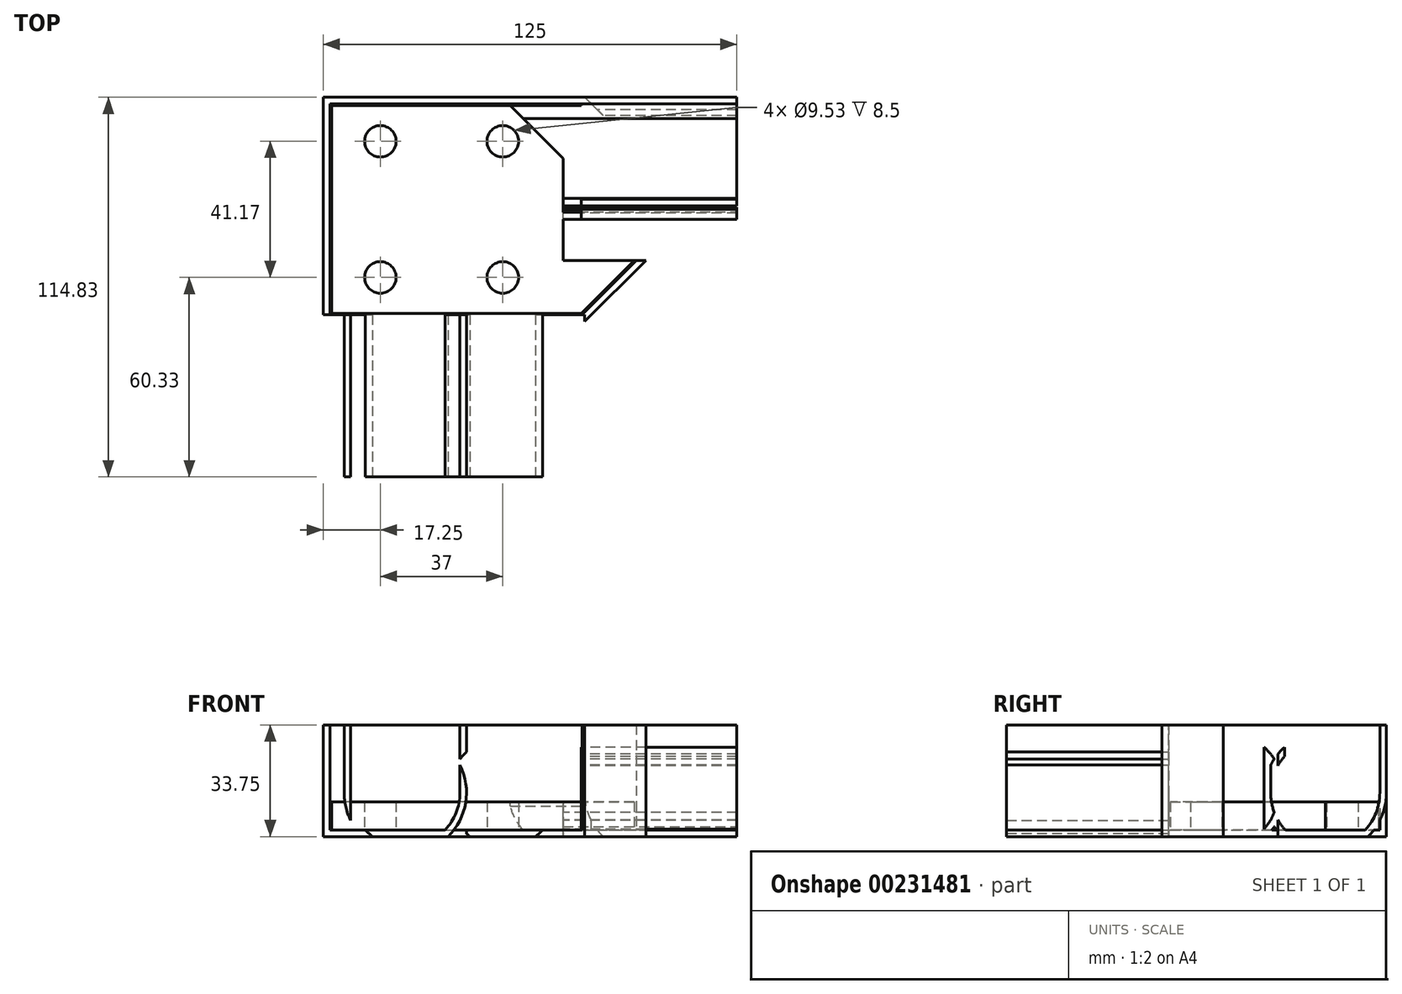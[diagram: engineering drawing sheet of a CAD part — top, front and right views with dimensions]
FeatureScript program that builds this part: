
annotation { "Feature Type Name" : "Feature", "Feature Type Description" : "" }
export const myFeature = defineFeature(function(context is Context, id is Id, definition is map)
    precondition{}
    {
        {
            var Q0;
            Q0=qCreatedBy(makeId("Top.planeOp"),FACE);
            var sketch = newSketch(context, id + "F0", { "sketchPlane" : qUnion([Q0])});
            skLineSegment(sketch, "E0.bottom", {"start": v(0, 0) * mm, "end": v(-75.5, 0) * mm});
            skLineSegment(sketch, "E0.top", {"start": v(0, 62.83) * mm, "end": v(-75.5, 62.83) * mm});
            skLineSegment(sketch, "E0.left", {"start": v(0, 0) * mm, "end": v(0, 62.83) * mm});
            skLineSegment(sketch, "E0.right", {"start": v(-75.5, 0) * mm, "end": v(-75.5, 62.83) * mm});
            skLineSegment(sketch, "E1", {"start": v(0, 62.83) * mm, "end": v(17, 45.83) * mm});
            skLineSegment(sketch, "E2", {"start": v(17, 45.83) * mm, "end": v(17, 17) * mm});
            skLineSegment(sketch, "E3", {"start": v(17, 17) * mm, "end": v(0, 0) * mm});
            skCircle(sketch, "E4", {"center": v(-23.75, 52) * mm, "radius": 4.76 * mm});
            skLineSegment(sketch, "E5", {"start": v(-75.5, 31.41) * mm, "end": v(0, 31.41) * mm, "construction": true});
            skCircle(sketch, "E6.1.0.0", {"center": v(-23.75, 10.83) * mm, "radius": 4.76 * mm});
            skLineSegment(sketch, "E6.direction1", {"start": v(-23.75, 52) * mm, "end": v(-23.75, 10.83) * mm, "construction": true});
            skCircle(sketch, "E7.1.0.0", {"center": v(-60.75, 52) * mm, "radius": 4.76 * mm});
            skCircle(sketch, "E7.1.0.1", {"center": v(-60.75, 10.83) * mm, "radius": 4.76 * mm});
            skLineSegment(sketch, "E7.direction1", {"start": v(-23.75, 52) * mm, "end": v(-60.75, 52) * mm, "construction": true});
            skSolve(sketch);
        }
        {
            var Q0;
            Q0=makeQuery(id+"F0.imprint","IMPRINT",FACE,{"disambiguationData":[TD([[makeQuery(id+"F0.imprint","IMPRINT",EDGE,{"derivedFrom":sQuery(id+"F0.wireOp",EDGE,"E0.bottom")}),-1.0]])]});
            var Q1;
            Q1=makeQuery(id+"F0.imprint","IMPRINT",FACE,{"disambiguationData":[TD([[makeQuery(id+"F0.imprint","IMPRINT",EDGE,{"derivedFrom":sQuery(id+"F0.wireOp",EDGE,"E0.left")}),-1.0]])]});
            extrude(context, id + "F1", {"entities" : qUnion([Q0, Q1]), "depth" : 10.5 * mm});
        }
        {
            var Q0;
            Q0=qCreatedBy(makeId("Top.planeOp"),FACE);
            var sketch = newSketch(context, id + "F2", { "sketchPlane" : qUnion([Q0])});
            skLineSegment(sketch, "E8.bottom", {"start": v(0.2, -0.5) * mm, "end": v(-76, -0.5) * mm});
            skLineSegment(sketch, "E8.top", {"start": v(0.2, 63.33) * mm, "end": v(-76, 63.33) * mm});
            skLineSegment(sketch, "E8.left", {"start": v(0.2, -0.5) * mm, "end": v(0.2, 63.33) * mm});
            skLineSegment(sketch, "E8.right", {"start": v(-76, -0.5) * mm, "end": v(-76, 63.33) * mm});
            skLineSegment(sketch, "E9", {"start": v(0.2, 63.33) * mm, "end": v(17.5, 46.04) * mm});
            skLineSegment(sketch, "E10", {"start": v(17.5, 46.04) * mm, "end": v(17.5, 16.8) * mm});
            skLineSegment(sketch, "E11", {"start": v(17.5, 16.8) * mm, "end": v(0.2, -0.5) * mm});
            skLineSegment(sketch, "E12", {"start": v(-76, 31.41) * mm, "end": v(0.2, 31.41) * mm, "construction": true});
            skLineSegment(sketch, "E13.bottom", {"start": v(1.04, -2.5) * mm, "end": v(-78, -2.5) * mm});
            skLineSegment(sketch, "E13.top", {"start": v(1.04, 65.33) * mm, "end": v(-78, 65.33) * mm});
            skLineSegment(sketch, "E13.left", {"start": v(1.04, -2.5) * mm, "end": v(1.04, 65.33) * mm});
            skLineSegment(sketch, "E13.right", {"start": v(-78, -2.5) * mm, "end": v(-78, 65.33) * mm});
            skLineSegment(sketch, "E14", {"start": v(1.04, 65.33) * mm, "end": v(19.5, 46.87) * mm});
            skLineSegment(sketch, "E15", {"start": v(19.5, 46.87) * mm, "end": v(19.5, 15.96) * mm});
            skLineSegment(sketch, "E16", {"start": v(19.5, 15.96) * mm, "end": v(1.04, -2.5) * mm});
            skSolve(sketch);
        }
        {
            var Q0;
            Q0 = qSketchRegion(id + "F2", true);
            var Q1;
            {var subQ0=sQuery(id+"F2.wireOp",EDGE,"E10");Q1=makeQuery(id+"F2.imprint","IMPRINT",FACE,{"disambiguationData":[TD([[makeQuery(id+"F2.imprint","IMPRINT",EDGE,{"derivedFrom":subQ0}),-1.0]])]});}
            var Q2;
            Q2=makeQuery(id+"F2.imprint","IMPRINT",FACE,{"disambiguationData":[TD([[makeQuery(id+"F2.imprint","IMPRINT",EDGE,{"derivedFrom":sQuery(id+"F2.wireOp",EDGE,"E8.bottom")}),-1.0]])]});
            var Q3;
            {var subQ0=sQuery(id+"F2.wireOp",EDGE,"E8.left");Q3=makeQuery(id+"F2.imprint","IMPRINT",FACE,{"disambiguationData":[TD([[makeQuery(id+"F2.imprint","IMPRINT",EDGE,{"derivedFrom":subQ0}),-1.0]])]});}
            extrude(context, id + "F3", {"entities" : qUnion([Q0, Q1, Q2, Q3]), "depth" : 2 * mm});
        }
        {
            var Q0;
            {var subQ5=sQuery(id+"F2.wireOp",EDGE,"E8.bottom");Q0=makeQuery(id+"F2.imprint","IMPRINT",FACE,{"disambiguationData":[TD([[makeQuery(id+"F2.imprint","IMPRINT",EDGE,{"derivedFrom":subQ5}),1.0]])]});}
            var Q1;
            {var subQ4=sQuery(id+"F2.wireOp",EDGE,"E10");Q1=makeQuery(id+"F2.imprint","IMPRINT",FACE,{"disambiguationData":[TD([[makeQuery(id+"F2.imprint","IMPRINT",EDGE,{"derivedFrom":subQ4}),1.0]])]});}
            extrude(context, id + "F4", {"entities" : qUnion([Q0, Q1]), "depth" : (21 + 10.75 + 2) * mm});
        }
        {
            var Q0;
            Q0=makeQuery(id+"F3.opExtrude","SWEPT_BODY",BODY,{"disambiguationData":[OSD([sQuery(id+"F2.wireOp",EDGE,"E13.bottom"),sQuery(id+"F2.wireOp",EDGE,"E13.top"),sQuery(id+"F2.wireOp",EDGE,"E13.right"),sQuery(id+"F2.wireOp",EDGE,"E14"),sQuery(id+"F2.wireOp",EDGE,"E15"),sQuery(id+"F2.wireOp",EDGE,"E16")])]});
            var Q1;
            Q1=makeQuery(id+"F4.opExtrude","SWEPT_BODY",BODY,{"disambiguationData":[OSD([sQuery(id+"F2.wireOp",EDGE,"E8.bottom"),sQuery(id+"F2.wireOp",EDGE,"E8.top"),sQuery(id+"F2.wireOp",EDGE,"E8.right"),sQuery(id+"F2.wireOp",EDGE,"E9"),sQuery(id+"F2.wireOp",EDGE,"E10"),sQuery(id+"F2.wireOp",EDGE,"E11"),sQuery(id+"F2.wireOp",EDGE,"E13.bottom"),sQuery(id+"F2.wireOp",EDGE,"E13.top"),sQuery(id+"F2.wireOp",EDGE,"E13.right"),sQuery(id+"F2.wireOp",EDGE,"E14"),sQuery(id+"F2.wireOp",EDGE,"E15"),sQuery(id+"F2.wireOp",EDGE,"E16")])]});
            booleanBodies(context, id + "F5", {"operationType" : BooleanOperationType.UNION, "tools" : qUnion([Q0, Q1])});
        }
        {
            var Q0;
            {var subQ0=sQuery(id+"F2.wireOp",EDGE,"E13.bottom");Q0=makeQuery(id+"F5.opBoolean","MERGE",FACE,{"derivedFrom":[makeQuery(id+"F3.opExtrude","SWEPT_FACE",FACE,{"disambiguationData":[OSD([subQ0])]}),makeQuery(id+"F4.opExtrude","SWEPT_FACE",FACE,{"disambiguationData":[OSD([subQ0])]})]});}
            var sketch = newSketch(context, id + "F6", { "sketchPlane" : qUnion([Q0])});
            skPoint(sketch, "E17.0", {"position": v(-23.75, 0) * mm});
            skPoint(sketch, "E18.0", {"position": v(-60.75, 0) * mm});
            skCircle(sketch, "E19", {"center": v(-23.75, 13.24) * mm, "radius": 18.5 * mm});
            skLineSegment(sketch, "E20", {"start": v(-23.75, 0) * mm, "end": v(-23.75, 33.75) * mm, "construction": true});
            skLineSegment(sketch, "E21", {"start": v(-42.25, 0) * mm, "end": v(-42.25, 33.75) * mm, "construction": true});
            skLineSegment(sketch, "E22", {"start": v(-60.75, 0) * mm, "end": v(-23.75, 0) * mm});
            skLineSegment(sketch, "E23", {"start": v(-42.25, 0) * mm, "end": v(-42.25, 33.75) * mm});
            skLineSegment(sketch, "E24", {"start": v(-5.25, 0) * mm, "end": v(-5.25, 33.75) * mm});
            skCircle(sketch, "E25", {"center": v(-23.75, 13.24) * mm, "radius": 16.5 * mm});
            skLineSegment(sketch, "E26", {"start": v(-40.25, 33.75) * mm, "end": v(-40.25, 0) * mm});
            skLineSegment(sketch, "E27", {"start": v(-7.25, 33.75) * mm, "end": v(-7.25, 0) * mm});
            skLineSegment(sketch, "E28", {"start": v(-42.25, 13.24) * mm, "end": v(-5.25, 13.24) * mm});
            skLineSegment(sketch, "E29", {"start": v(-35.83, 2) * mm, "end": v(-11.67, 2) * mm});
            skLineSegment(sketch, "E30", {"start": v(-38.48, 33.75) * mm, "end": v(-38.48, 0) * mm, "construction": true});
            skLineSegment(sketch, "E31.MirrorCS", {"start": v(-34.71, 0) * mm, "end": v(-34.71, 33.75) * mm});
            skLineSegment(sketch, "E32.MirrorCS", {"start": v(-41.13, 2) * mm, "end": v(-65.3, 2) * mm});
            skLineSegment(sketch, "E33.MirrorCS", {"start": v(-69.71, 33.75) * mm, "end": v(-69.71, 0) * mm});
            skLineSegment(sketch, "E34.MirrorCS", {"start": v(-36.71, 33.75) * mm, "end": v(-36.71, 0) * mm});
            skPoint(sketch, "E35.MirrorP", {"position": v(-53.21, 0) * mm});
            skCircle(sketch, "E36.MirrorC", {"center": v(-53.21, 13.24) * mm, "radius": 16.5 * mm});
            skLineSegment(sketch, "E37.MirrorCS", {"start": v(-71.71, 0) * mm, "end": v(-71.71, 33.75) * mm});
            skCircle(sketch, "E38.MirrorC", {"center": v(-53.21, 13.24) * mm, "radius": 18.5 * mm});
            skLineSegment(sketch, "E39.MirrorCS", {"start": v(-53.21, 0) * mm, "end": v(-53.21, 33.75) * mm, "construction": true});
            skLineSegment(sketch, "E40.MirrorCS", {"start": v(-34.71, 0) * mm, "end": v(-34.71, 33.75) * mm, "construction": true});
            skLineSegment(sketch, "E41.MirrorCS", {"start": v(-34.71, 13.24) * mm, "end": v(-71.71, 13.24) * mm});
            skSolve(sketch);
        }
        {
            var Q0;
            {var subQ0=sQuery(id+"F2.wireOp",EDGE,"E13.right");Q0=makeQuery(id+"F5.opBoolean","MERGE",FACE,{"derivedFrom":[makeQuery(id+"F3.opExtrude","SWEPT_FACE",FACE,{"disambiguationData":[OSD([subQ0])]}),makeQuery(id+"F4.opExtrude","SWEPT_FACE",FACE,{"disambiguationData":[OSD([subQ0])]})]});}
            cPlane(context, id + "F7", {"entities" : qUnion([Q0]), "cplaneType" : CPlaneType.OFFSET, "offset" : 78 * mm, "oppositeDirection" : true, "width" : 150 * mm, "height" : 150 * mm});
        }
        {
            var Q0;
            Q0=qCreatedBy(id+"F7.planeOp",FACE);
            var sketch = newSketch(context, id + "F8", { "sketchPlane" : qUnion([Q0])});
            skPoint(sketch, "E42.0", {"position": v(0.5, 33.75) * mm});
            skPoint(sketch, "E43.0", {"position": v(-63.33, 33.75) * mm});
            skCircle(sketch, "E44", {"center": v(-16, 13.24) * mm, "radius": 18.5 * mm});
            skLineSegment(sketch, "E45", {"start": v(0.5, 33.75) * mm, "end": v(0.5, 0) * mm});
            skLineSegment(sketch, "E46.bottom", {"start": v(-34.5, 33.75) * mm, "end": v(-32.5, 33.75) * mm});
            skLineSegment(sketch, "E46.top", {"start": v(-34.5, 0) * mm, "end": v(-32.5, 0) * mm});
            skLineSegment(sketch, "E46.left", {"start": v(-34.5, 33.75) * mm, "end": v(-34.5, 0) * mm});
            skLineSegment(sketch, "E46.right", {"start": v(-32.5, 33.75) * mm, "end": v(-32.5, 0) * mm});
            skLineSegment(sketch, "E47.bottom", {"start": v(-32.5, 2) * mm, "end": v(0.5, 2) * mm});
            skLineSegment(sketch, "E47.top", {"start": v(-32.5, 0) * mm, "end": v(0.5, 0) * mm});
            skLineSegment(sketch, "E47.left", {"start": v(-32.5, 2) * mm, "end": v(-32.5, 0) * mm});
            skLineSegment(sketch, "E47.right", {"start": v(0.5, 2) * mm, "end": v(0.5, 0) * mm});
            skCircle(sketch, "E48", {"center": v(-16, 13.24) * mm, "radius": 16.5 * mm});
            skLineSegment(sketch, "E49", {"start": v(0.5, 33.75) * mm, "end": v(2.5, 33.75) * mm});
            skLineSegment(sketch, "E50", {"start": v(2.5, 33.75) * mm, "end": v(2.5, 0) * mm});
            skLineSegment(sketch, "E51", {"start": v(2.5, 0) * mm, "end": v(0.5, 0) * mm});
            skLineSegment(sketch, "E52", {"start": v(0.5, 33.75) * mm, "end": v(-32.5, 33.75) * mm});
            skLineSegment(sketch, "E53", {"start": v(-31.41, 34.55) * mm, "end": v(-31.41, 0) * mm, "construction": true});
            skLineSegment(sketch, "E54.MirrorCS", {"start": v(-30.33, 2) * mm, "end": v(-30.33, 0) * mm});
            skLineSegment(sketch, "E55.MirrorCS", {"start": v(-63.33, 33.75) * mm, "end": v(-65.33, 33.75) * mm});
            skLineSegment(sketch, "E56.MirrorCS", {"start": v(-63.33, 2) * mm, "end": v(-63.33, 0) * mm});
            skLineSegment(sketch, "E57.MirrorCS", {"start": v(-28.33, 33.75) * mm, "end": v(-30.33, 33.75) * mm});
            skLineSegment(sketch, "E58.MirrorCS", {"start": v(-30.33, 2) * mm, "end": v(-63.33, 2) * mm});
            skLineSegment(sketch, "E59.MirrorCS", {"start": v(-28.33, 33.75) * mm, "end": v(-28.33, 0) * mm});
            skCircle(sketch, "E60.MirrorC", {"center": v(-46.83, 13.24) * mm, "radius": 16.5 * mm});
            skLineSegment(sketch, "E61.MirrorCS", {"start": v(-65.33, 33.75) * mm, "end": v(-65.33, 0) * mm});
            skLineSegment(sketch, "E62.MirrorCS", {"start": v(-63.33, 33.75) * mm, "end": v(-30.33, 33.75) * mm});
            skLineSegment(sketch, "E63.MirrorCS", {"start": v(-30.33, 0) * mm, "end": v(-63.33, 0) * mm});
            skLineSegment(sketch, "E64.MirrorCS", {"start": v(-28.33, 0) * mm, "end": v(-30.33, 0) * mm});
            skLineSegment(sketch, "E65.MirrorCS", {"start": v(-63.33, 33.75) * mm, "end": v(-63.33, 0) * mm});
            skCircle(sketch, "E66.MirrorC", {"center": v(-46.83, 13.24) * mm, "radius": 18.5 * mm});
            skLineSegment(sketch, "E67.MirrorCS", {"start": v(-65.33, 0) * mm, "end": v(-63.33, 0) * mm});
            skLineSegment(sketch, "E68.MirrorCS", {"start": v(-30.33, 33.75) * mm, "end": v(-30.33, 0) * mm});
            skSolve(sketch);
        }
        {
            var Q0;
            {var subQ0=sQuery(id+"F6.wireOp",EDGE,"E33.MirrorCS");var subQ1=makeQuery(id+"F4.opExtrude","CAP_EDGE",EDGE,{"disambiguationData":[OSD([sQuery(id+"F2.wireOp",EDGE,"E13.bottom")])],"isStart":false});var subQ2=makeQuery(id+"F6.imprint","INTERSECT",VERTEX,{"derivedFrom":[subQ1,subQ0]});Q0=makeQuery(id+"F6.imprint","IMPRINT",FACE,{"disambiguationData":[TD([[makeQuery(id+"F6.imprint","IMPRINT",EDGE,{"disambiguationData":[TD([[subQ2,-1.0]])],"derivedFrom":subQ0}),-1.0]])]});}
            var Q1;
            {var subQ0=sQuery(id+"F6.wireOp",EDGE,"E38.MirrorC");var subQ1=sQuery(id+"F6.wireOp",EDGE,"E33.MirrorCS");var subQ2=makeQuery(id+"F6.imprint","INTERSECT",VERTEX,{"disambiguationData":[OD(0.0)],"derivedFrom":[subQ1,subQ0]});Q1=makeQuery(id+"F6.imprint","IMPRINT",FACE,{"disambiguationData":[TD([[makeQuery(id+"F6.imprint","IMPRINT",EDGE,{"disambiguationData":[TD([[subQ2,-1.0]])],"derivedFrom":subQ1}),-1.0]])]});}
            var Q2;
            {var subQ0=sQuery(id+"F6.wireOp",EDGE,"E38.MirrorC");var subQ1=sQuery(id+"F6.wireOp",EDGE,"E33.MirrorCS");var subQ2=makeQuery(id+"F6.imprint","INTERSECT",VERTEX,{"disambiguationData":[OD(1.0)],"derivedFrom":[subQ1,subQ0]});Q2=makeQuery(id+"F6.imprint","IMPRINT",FACE,{"disambiguationData":[TD([[makeQuery(id+"F6.imprint","IMPRINT",EDGE,{"disambiguationData":[TD([[subQ2,1.0]])],"derivedFrom":subQ1}),-1.0]])]});}
            var Q3;
            {var subQ5=sQuery(id+"F6.wireOp",EDGE,"E36.MirrorC");var subQ7=makeQuery(id+"F6.imprint","INTERSECT",VERTEX,{"disambiguationData":[OD(1.0)],"derivedFrom":[sQuery(id+"F6.wireOp",EDGE,"E32.MirrorCS"),subQ5]});Q3=makeQuery(id+"F6.imprint","IMPRINT",FACE,{"disambiguationData":[TD([[makeQuery(id+"F6.imprint","IMPRINT",EDGE,{"disambiguationData":[TD([[subQ7,1.0]])],"derivedFrom":subQ5}),1.0]])]});}
            var Q4;
            {var subQ1=sQuery(id+"F6.wireOp",EDGE,"E22");var subQ8=makeQuery(id+"F3.opExtrude","CAP_EDGE",EDGE,{"disambiguationData":[OSD([sQuery(id+"F2.wireOp",EDGE,"E13.bottom")])],"isStart":true});var subQ9=makeQuery(id+"F6.imprint","INTERSECT",VERTEX,{"disambiguationData":[OD(1.0)],"derivedFrom":[subQ8,subQ1]});Q4=makeQuery(id+"F6.imprint","IMPRINT",FACE,{"disambiguationData":[TD([[makeQuery(id+"F6.imprint","IMPRINT",EDGE,{"disambiguationData":[TD([[subQ9,1.0]])],"derivedFrom":subQ1}),-1.0]])]});}
            var Q5;
            {var subQ0=sQuery(id+"F6.wireOp",EDGE,"E36.MirrorC");var subQ1=sQuery(id+"F6.wireOp",EDGE,"E23");var subQ2=makeQuery(id+"F6.imprint","INTERSECT",VERTEX,{"disambiguationData":[OD(0.0)],"derivedFrom":[subQ1,subQ0]});Q5=makeQuery(id+"F6.imprint","IMPRINT",FACE,{"disambiguationData":[TD([[makeQuery(id+"F6.imprint","IMPRINT",EDGE,{"disambiguationData":[TD([[subQ2,-1.0]])],"derivedFrom":subQ1}),-1.0]])]});}
            var Q6;
            {var subQ6=sQuery(id+"F6.wireOp",EDGE,"E23");var subQ7=sQuery(id+"F6.wireOp",EDGE,"E22");var subQ8=makeQuery(id+"F6.imprint","INTERSECT",VERTEX,{"derivedFrom":[subQ7,subQ6]});Q6=makeQuery(id+"F6.imprint","IMPRINT",FACE,{"disambiguationData":[TD([[makeQuery(id+"F6.imprint","IMPRINT",EDGE,{"disambiguationData":[TD([[subQ8,1.0]])],"derivedFrom":subQ7}),-1.0]])]});}
            var Q7;
            {var subQ0=sQuery(id+"F6.wireOp",EDGE,"E23");var subQ1=sQuery(id+"F6.wireOp",EDGE,"E22");var subQ2=makeQuery(id+"F6.imprint","INTERSECT",VERTEX,{"derivedFrom":[subQ1,subQ0]});Q7=makeQuery(id+"F6.imprint","IMPRINT",FACE,{"disambiguationData":[TD([[makeQuery(id+"F6.imprint","IMPRINT",EDGE,{"disambiguationData":[TD([[subQ2,-1.0]])],"derivedFrom":subQ1}),-1.0]])]});}
            var Q8;
            {var subQ0=sQuery(id+"F6.wireOp",EDGE,"E36.MirrorC");var subQ1=sQuery(id+"F6.wireOp",EDGE,"E19");var subQ2=makeQuery(id+"F6.imprint","INTERSECT",VERTEX,{"disambiguationData":[OD(1.0)],"derivedFrom":[subQ1,subQ0]});Q8=makeQuery(id+"F6.imprint","IMPRINT",FACE,{"disambiguationData":[TD([[makeQuery(id+"F6.imprint","IMPRINT",EDGE,{"disambiguationData":[TD([[subQ2,-1.0]])],"derivedFrom":subQ1}),-1.0]])]});}
            var Q9;
            {var subQ0=sQuery(id+"F6.wireOp",EDGE,"E36.MirrorC");var subQ1=sQuery(id+"F6.wireOp",EDGE,"E19");var subQ2=makeQuery(id+"F6.imprint","INTERSECT",VERTEX,{"disambiguationData":[OD(1.0)],"derivedFrom":[subQ1,subQ0]});Q9=makeQuery(id+"F6.imprint","IMPRINT",FACE,{"disambiguationData":[TD([[makeQuery(id+"F6.imprint","IMPRINT",EDGE,{"disambiguationData":[TD([[subQ2,-1.0]])],"derivedFrom":subQ1}),1.0]])]});}
            var Q10;
            {var subQ0=sQuery(id+"F6.wireOp",EDGE,"E36.MirrorC");var subQ1=sQuery(id+"F6.wireOp",EDGE,"E25");var subQ2=makeQuery(id+"F6.imprint","INTERSECT",VERTEX,{"disambiguationData":[OD(1.0)],"derivedFrom":[subQ1,subQ0]});Q10=makeQuery(id+"F6.imprint","IMPRINT",FACE,{"disambiguationData":[TD([[makeQuery(id+"F6.imprint","IMPRINT",EDGE,{"disambiguationData":[TD([[subQ2,-1.0]])],"derivedFrom":subQ1}),1.0]])]});}
            var Q11;
            {var subQ0=sQuery(id+"F6.wireOp",EDGE,"E38.MirrorC");var subQ1=sQuery(id+"F6.wireOp",EDGE,"E34.MirrorCS");var subQ2=makeQuery(id+"F6.imprint","INTERSECT",VERTEX,{"disambiguationData":[OD(1.0)],"derivedFrom":[subQ1,subQ0]});Q11=makeQuery(id+"F6.imprint","IMPRINT",FACE,{"disambiguationData":[TD([[makeQuery(id+"F6.imprint","IMPRINT",EDGE,{"disambiguationData":[TD([[subQ2,1.0]])],"derivedFrom":subQ1}),1.0]])]});}
            var Q12;
            {var subQ0=sQuery(id+"F6.wireOp",EDGE,"E38.MirrorC");var subQ1=sQuery(id+"F6.wireOp",EDGE,"E34.MirrorCS");var subQ2=makeQuery(id+"F6.imprint","INTERSECT",VERTEX,{"disambiguationData":[OD(0.0)],"derivedFrom":[subQ1,subQ0]});Q12=makeQuery(id+"F6.imprint","IMPRINT",FACE,{"disambiguationData":[TD([[makeQuery(id+"F6.imprint","IMPRINT",EDGE,{"disambiguationData":[TD([[subQ2,-1.0]])],"derivedFrom":subQ1}),1.0]])]});}
            var Q13;
            {var subQ0=sQuery(id+"F6.wireOp",EDGE,"E31.MirrorCS");var subQ1=sQuery(id+"F6.wireOp",EDGE,"E25");var subQ2=makeQuery(id+"F6.imprint","INTERSECT",VERTEX,{"disambiguationData":[OD(0.0)],"derivedFrom":[subQ1,subQ0]});Q13=makeQuery(id+"F6.imprint","IMPRINT",FACE,{"disambiguationData":[TD([[makeQuery(id+"F6.imprint","IMPRINT",EDGE,{"disambiguationData":[TD([[subQ2,-1.0]])],"derivedFrom":subQ1}),1.0]])]});}
            var Q14;
            {var subQ0=sQuery(id+"F6.wireOp",EDGE,"E31.MirrorCS");var subQ1=sQuery(id+"F6.wireOp",EDGE,"E19");var subQ2=makeQuery(id+"F6.imprint","INTERSECT",VERTEX,{"derivedFrom":[subQ1,subQ0]});Q14=makeQuery(id+"F6.imprint","IMPRINT",FACE,{"disambiguationData":[TD([[makeQuery(id+"F6.imprint","IMPRINT",EDGE,{"disambiguationData":[TD([[subQ2,-1.0]])],"derivedFrom":subQ1}),1.0]])]});}
            var Q15;
            {var subQ0=sQuery(id+"F6.wireOp",EDGE,"E31.MirrorCS");var subQ1=sQuery(id+"F6.wireOp",EDGE,"E19");var subQ2=makeQuery(id+"F6.imprint","INTERSECT",VERTEX,{"derivedFrom":[subQ1,subQ0]});Q15=makeQuery(id+"F6.imprint","IMPRINT",FACE,{"disambiguationData":[TD([[makeQuery(id+"F6.imprint","IMPRINT",EDGE,{"disambiguationData":[TD([[subQ2,-1.0]])],"derivedFrom":subQ1}),-1.0]])]});}
            extrude(context, id + "F9", {"entities" : qUnion([Q0, Q1, Q2, Q3, Q4, Q5, Q6, Q7, Q8, Q9, Q10, Q11, Q12, Q13, Q14, Q15]), "operationType" : NewBodyOperationType.ADD, "depth" : 47 * mm});
        }
        {
            var Q0;
            {var subQ0=sQuery(id+"F8.wireOp",EDGE,"E66.MirrorC");var subQ1=sQuery(id+"F8.wireOp",EDGE,"E48");var subQ2=makeQuery(id+"F8.imprint","INTERSECT",VERTEX,{"disambiguationData":[OD(0.0)],"derivedFrom":[subQ1,subQ0]});Q0=makeQuery(id+"F8.imprint","IMPRINT",FACE,{"disambiguationData":[TD([[makeQuery(id+"F8.imprint","IMPRINT",EDGE,{"disambiguationData":[TD([[subQ2,-1.0]])],"derivedFrom":subQ1}),1.0]])]});}
            var Q1;
            {var subQ0=sQuery(id+"F8.wireOp",EDGE,"E60.MirrorC");var subQ1=sQuery(id+"F8.wireOp",EDGE,"E48");var subQ2=makeQuery(id+"F8.imprint","INTERSECT",VERTEX,{"disambiguationData":[OD(1.0)],"derivedFrom":[subQ1,subQ0]});Q1=makeQuery(id+"F8.imprint","IMPRINT",FACE,{"disambiguationData":[TD([[makeQuery(id+"F8.imprint","IMPRINT",EDGE,{"disambiguationData":[TD([[subQ2,-1.0]])],"derivedFrom":subQ1}),1.0]])]});}
            var Q2;
            {var subQ0=sQuery(id+"F8.wireOp",EDGE,"E59.MirrorCS");var subQ1=sQuery(id+"F8.wireOp",EDGE,"E48");var subQ2=makeQuery(id+"F8.imprint","INTERSECT",VERTEX,{"disambiguationData":[OD(0.0)],"derivedFrom":[subQ1,subQ0]});Q2=makeQuery(id+"F8.imprint","IMPRINT",FACE,{"disambiguationData":[TD([[makeQuery(id+"F8.imprint","IMPRINT",EDGE,{"disambiguationData":[TD([[subQ2,-1.0]])],"derivedFrom":subQ1}),1.0]])]});}
            var Q3;
            {var subQ0=sQuery(id+"F8.wireOp",EDGE,"E59.MirrorCS");var subQ1=sQuery(id+"F8.wireOp",EDGE,"E44");var subQ2=makeQuery(id+"F8.imprint","INTERSECT",VERTEX,{"derivedFrom":[subQ1,subQ0]});Q3=makeQuery(id+"F8.imprint","IMPRINT",FACE,{"disambiguationData":[TD([[makeQuery(id+"F8.imprint","IMPRINT",EDGE,{"disambiguationData":[TD([[subQ2,-1.0]])],"derivedFrom":subQ1}),1.0]])]});}
            var Q4;
            {var subQ5=sQuery(id+"F8.wireOp",EDGE,"E57.MirrorCS");Q4=makeQuery(id+"F8.imprint","IMPRINT",FACE,{"disambiguationData":[TD([[makeQuery(id+"F8.imprint","IMPRINT",EDGE,{"derivedFrom":subQ5}),1.0]])]});}
            var Q5;
            {var subQ5=sQuery(id+"F8.wireOp",EDGE,"E46.right");var subQ6=sQuery(id+"F8.wireOp",EDGE,"E44");var subQ7=makeQuery(id+"F8.imprint","INTERSECT",VERTEX,{"disambiguationData":[OD(1.0)],"derivedFrom":[subQ6,subQ5]});Q5=makeQuery(id+"F8.imprint","IMPRINT",FACE,{"disambiguationData":[TD([[makeQuery(id+"F8.imprint","IMPRINT",EDGE,{"disambiguationData":[TD([[subQ7,-1.0]])],"derivedFrom":subQ6}),1.0]])]});}
            var Q6;
            {var subQ5=sQuery(id+"F8.wireOp",EDGE,"E44");var subQ7=sQuery(id+"F8.wireOp",EDGE,"E60.MirrorC");var subQ9=makeQuery(id+"F8.imprint","INTERSECT",VERTEX,{"disambiguationData":[OD(1.0)],"derivedFrom":[subQ5,subQ7]});Q6=makeQuery(id+"F8.imprint","IMPRINT",FACE,{"disambiguationData":[TD([[makeQuery(id+"F8.imprint","IMPRINT",EDGE,{"disambiguationData":[TD([[subQ9,-1.0]])],"derivedFrom":subQ5}),-1.0]])]});}
            var Q7;
            {var subQ0=sQuery(id+"F8.wireOp",EDGE,"E46.right");var subQ1=sQuery(id+"F8.wireOp",EDGE,"E44");var subQ2=makeQuery(id+"F8.imprint","INTERSECT",VERTEX,{"disambiguationData":[OD(1.0)],"derivedFrom":[subQ1,subQ0]});Q7=makeQuery(id+"F8.imprint","IMPRINT",FACE,{"disambiguationData":[TD([[makeQuery(id+"F8.imprint","IMPRINT",EDGE,{"disambiguationData":[TD([[subQ2,-1.0]])],"derivedFrom":subQ1}),-1.0]])]});}
            var Q8;
            {var subQ0=sQuery(id+"F8.wireOp",EDGE,"E63.MirrorCS");var subQ1=sQuery(id+"F8.wireOp",EDGE,"E46.left");var subQ2=makeQuery(id+"F8.imprint","INTERSECT",VERTEX,{"derivedFrom":[subQ1,subQ0]});Q8=makeQuery(id+"F8.imprint","IMPRINT",FACE,{"disambiguationData":[TD([[makeQuery(id+"F8.imprint","IMPRINT",EDGE,{"disambiguationData":[TD([[subQ2,1.0]])],"derivedFrom":subQ1}),1.0]])]});}
            var Q9;
            {var subQ0=sQuery(id+"F8.wireOp",EDGE,"E63.MirrorCS");var subQ1=sQuery(id+"F8.wireOp",EDGE,"E46.left");var subQ2=makeQuery(id+"F8.imprint","INTERSECT",VERTEX,{"derivedFrom":[subQ1,subQ0]});Q9=makeQuery(id+"F8.imprint","IMPRINT",FACE,{"disambiguationData":[TD([[makeQuery(id+"F8.imprint","IMPRINT",EDGE,{"disambiguationData":[TD([[subQ2,1.0]])],"derivedFrom":subQ1}),-1.0]])]});}
            var Q10;
            {var subQ0=sQuery(id+"F8.wireOp",EDGE,"E60.MirrorC");var subQ1=sQuery(id+"F8.wireOp",EDGE,"E58.MirrorCS");var subQ2=makeQuery(id+"F8.imprint","INTERSECT",VERTEX,{"disambiguationData":[OD(0.0)],"derivedFrom":[subQ1,subQ0]});Q10=makeQuery(id+"F8.imprint","IMPRINT",FACE,{"disambiguationData":[TD([[makeQuery(id+"F8.imprint","IMPRINT",EDGE,{"disambiguationData":[TD([[subQ2,-1.0]])],"derivedFrom":subQ1}),1.0]])]});}
            var Q11;
            {var subQ0=sQuery(id+"F8.wireOp",EDGE,"E60.MirrorC");var subQ1=sQuery(id+"F8.wireOp",EDGE,"E58.MirrorCS");var subQ2=makeQuery(id+"F8.imprint","INTERSECT",VERTEX,{"disambiguationData":[OD(1.0)],"derivedFrom":[subQ1,subQ0]});Q11=makeQuery(id+"F8.imprint","IMPRINT",FACE,{"disambiguationData":[TD([[makeQuery(id+"F8.imprint","IMPRINT",EDGE,{"disambiguationData":[TD([[subQ2,-1.0]])],"derivedFrom":subQ1}),1.0]])]});}
            var Q12;
            {var subQ0=sQuery(id+"F8.wireOp",EDGE,"E60.MirrorC");var subQ1=sQuery(id+"F8.wireOp",EDGE,"E58.MirrorCS");var subQ2=makeQuery(id+"F8.imprint","INTERSECT",VERTEX,{"disambiguationData":[OD(1.0)],"derivedFrom":[subQ1,subQ0]});Q12=makeQuery(id+"F8.imprint","IMPRINT",FACE,{"disambiguationData":[TD([[makeQuery(id+"F8.imprint","IMPRINT",EDGE,{"disambiguationData":[TD([[subQ2,-1.0]])],"derivedFrom":subQ1}),-1.0]])]});}
            var Q13;
            {var subQ0=sQuery(id+"F8.wireOp",EDGE,"E65.MirrorCS");var subQ1=makeQuery(id+"F8.imprint","INTERSECT",VERTEX,{"derivedFrom":[sQuery(id+"F8.wireOp",EDGE,"E60.MirrorC"),subQ0]});Q13=makeQuery(id+"F8.imprint","IMPRINT",FACE,{"disambiguationData":[TD([[makeQuery(id+"F8.imprint","IMPRINT",EDGE,{"disambiguationData":[TD([[subQ1,1.0]])],"derivedFrom":subQ0}),-1.0]])]});}
            var Q14;
            {var subQ0=sQuery(id+"F8.wireOp",EDGE,"E55.MirrorCS");Q14=makeQuery(id+"F8.imprint","IMPRINT",FACE,{"disambiguationData":[TD([[makeQuery(id+"F8.imprint","IMPRINT",EDGE,{"derivedFrom":subQ0}),1.0]])]});}
            var Q15;
            {var subQ0=sQuery(id+"F8.wireOp",EDGE,"E60.MirrorC");var subQ1=sQuery(id+"F8.wireOp",EDGE,"E46.left");var subQ2=makeQuery(id+"F8.imprint","INTERSECT",VERTEX,{"disambiguationData":[OD(1.0)],"derivedFrom":[subQ1,subQ0]});Q15=makeQuery(id+"F8.imprint","IMPRINT",FACE,{"disambiguationData":[TD([[makeQuery(id+"F8.imprint","IMPRINT",EDGE,{"disambiguationData":[TD([[subQ2,-1.0]])],"derivedFrom":subQ1}),-1.0]])]});}
            var Q16;
            {var subQ0=sQuery(id+"F8.wireOp",EDGE,"E66.MirrorC");var subQ1=sQuery(id+"F8.wireOp",EDGE,"E48");var subQ2=makeQuery(id+"F8.imprint","INTERSECT",VERTEX,{"disambiguationData":[OD(0.0)],"derivedFrom":[subQ1,subQ0]});Q16=makeQuery(id+"F8.imprint","IMPRINT",FACE,{"disambiguationData":[TD([[makeQuery(id+"F8.imprint","IMPRINT",EDGE,{"disambiguationData":[TD([[subQ2,-1.0]])],"derivedFrom":subQ1}),-1.0]])]});}
            var Q17;
            {var subQ0=sQuery(id+"F8.wireOp",EDGE,"E68.MirrorCS");var subQ1=sQuery(id+"F8.wireOp",EDGE,"E48");var subQ2=makeQuery(id+"F8.imprint","INTERSECT",VERTEX,{"disambiguationData":[OD(1.0)],"derivedFrom":[subQ1,subQ0]});Q17=makeQuery(id+"F8.imprint","IMPRINT",FACE,{"disambiguationData":[TD([[makeQuery(id+"F8.imprint","IMPRINT",EDGE,{"disambiguationData":[TD([[subQ2,-1.0]])],"derivedFrom":subQ1}),-1.0]])]});}
            var Q18;
            {var subQ0=sQuery(id+"F8.wireOp",EDGE,"E60.MirrorC");var subQ1=sQuery(id+"F8.wireOp",EDGE,"E44");var subQ2=makeQuery(id+"F8.imprint","INTERSECT",VERTEX,{"disambiguationData":[OD(1.0)],"derivedFrom":[subQ1,subQ0]});Q18=makeQuery(id+"F8.imprint","IMPRINT",FACE,{"disambiguationData":[TD([[makeQuery(id+"F8.imprint","IMPRINT",EDGE,{"disambiguationData":[TD([[subQ2,-1.0]])],"derivedFrom":subQ1}),1.0]])]});}
            var Q19;
            {var subQ1=sQuery(id+"F8.wireOp",EDGE,"E47.left");var subQ3=sQuery(id+"F8.wireOp",EDGE,"E66.MirrorC");var subQ4=makeQuery(id+"F8.imprint","INTERSECT",VERTEX,{"derivedFrom":[subQ1,subQ3]});Q19=makeQuery(id+"F8.imprint","IMPRINT",FACE,{"disambiguationData":[TD([[makeQuery(id+"F8.imprint","IMPRINT",EDGE,{"disambiguationData":[TD([[subQ4,1.0]])],"derivedFrom":subQ3}),-1.0]])]});}
            extrude(context, id + "F10", {"entities" : qUnion([Q0, Q1, Q2, Q3, Q4, Q5, Q6, Q7, Q8, Q9, Q10, Q11, Q12, Q13, Q14, Q15, Q16, Q17, Q18, Q19]), "operationType" : NewBodyOperationType.ADD, "oppositeDirection" : true, "depth" : 47 * mm});
        }
        {
            var Q0;
            {var subQ2=sQuery(id+"F6.wireOp",EDGE,"E32.MirrorCS");var subQ3=sQuery(id+"F2.wireOp",EDGE,"E13.bottom");Q0=makeQuery(id+"F9.boolean.opBoolean","SPLIT",FACE,{"disambiguationData":[TD([makeQuery(id+"F9.opExtrude","SWEPT_FACE",FACE,{"disambiguationData":[OSD([subQ2])]})])],"derivedFrom":makeQuery(id+"F5.opBoolean","MERGE",FACE,{"derivedFrom":[makeQuery(id+"F3.opExtrude","SWEPT_FACE",FACE,{"disambiguationData":[OSD([subQ3])]}),makeQuery(id+"F4.opExtrude","SWEPT_FACE",FACE,{"disambiguationData":[OSD([subQ3])]})]})});}
            var Q1;
            Q1=makeQuery(id+"F4.opExtrude","SWEPT_FACE",FACE,{"disambiguationData":[OSD([sQuery(id+"F2.wireOp",EDGE,"E8.bottom")])]});
            extrude(context, id + "F11", {"entities" : qUnion([Q0]), "operationType" : NewBodyOperationType.REMOVE, "endBound" : BoundingType.UP_TO_SURFACE, "oppositeDirection" : true, "endBoundEntityFace" : qUnion([Q1]), "depth" : 25 * mm});
        }
        {
            var Q0;
            {var subQ10=sQuery(id+"F2.wireOp",EDGE,"E14");var subQ11=sQuery(id+"F2.wireOp",EDGE,"E15");Q0=makeQuery(id+"F10.boolean.opBoolean","SPLIT",FACE,{"disambiguationData":[TD([makeQuery(id+"F3.opExtrude","SWEPT_FACE",FACE,{"disambiguationData":[OSD([subQ10])]})])],"derivedFrom":makeQuery(id+"F5.opBoolean","MERGE",FACE,{"derivedFrom":[makeQuery(id+"F3.opExtrude","SWEPT_FACE",FACE,{"disambiguationData":[OSD([subQ11])]}),makeQuery(id+"F4.opExtrude","SWEPT_FACE",FACE,{"disambiguationData":[OSD([subQ11])]})]})});}
            var Q1;
            {var subQ2=sQuery(id+"F2.wireOp",EDGE,"E15");var subQ3=sQuery(id+"F2.wireOp",EDGE,"E14");Q1=makeQuery(id+"F10.boolean.opBoolean","SPLIT",FACE,{"disambiguationData":[TD([makeQuery(id+"F3.opExtrude","SWEPT_FACE",FACE,{"disambiguationData":[OSD([subQ2])]})])],"derivedFrom":makeQuery(id+"F5.opBoolean","MERGE",FACE,{"derivedFrom":[makeQuery(id+"F3.opExtrude","SWEPT_FACE",FACE,{"disambiguationData":[OSD([subQ3])]}),makeQuery(id+"F4.opExtrude","SWEPT_FACE",FACE,{"disambiguationData":[OSD([subQ3])]})]})});}
            extrude(context, id + "F12", {"entities" : qUnion([Q0, Q1]), "operationType" : NewBodyOperationType.REMOVE, "oppositeDirection" : true, "depth" : 25 * mm});
        }
    });
